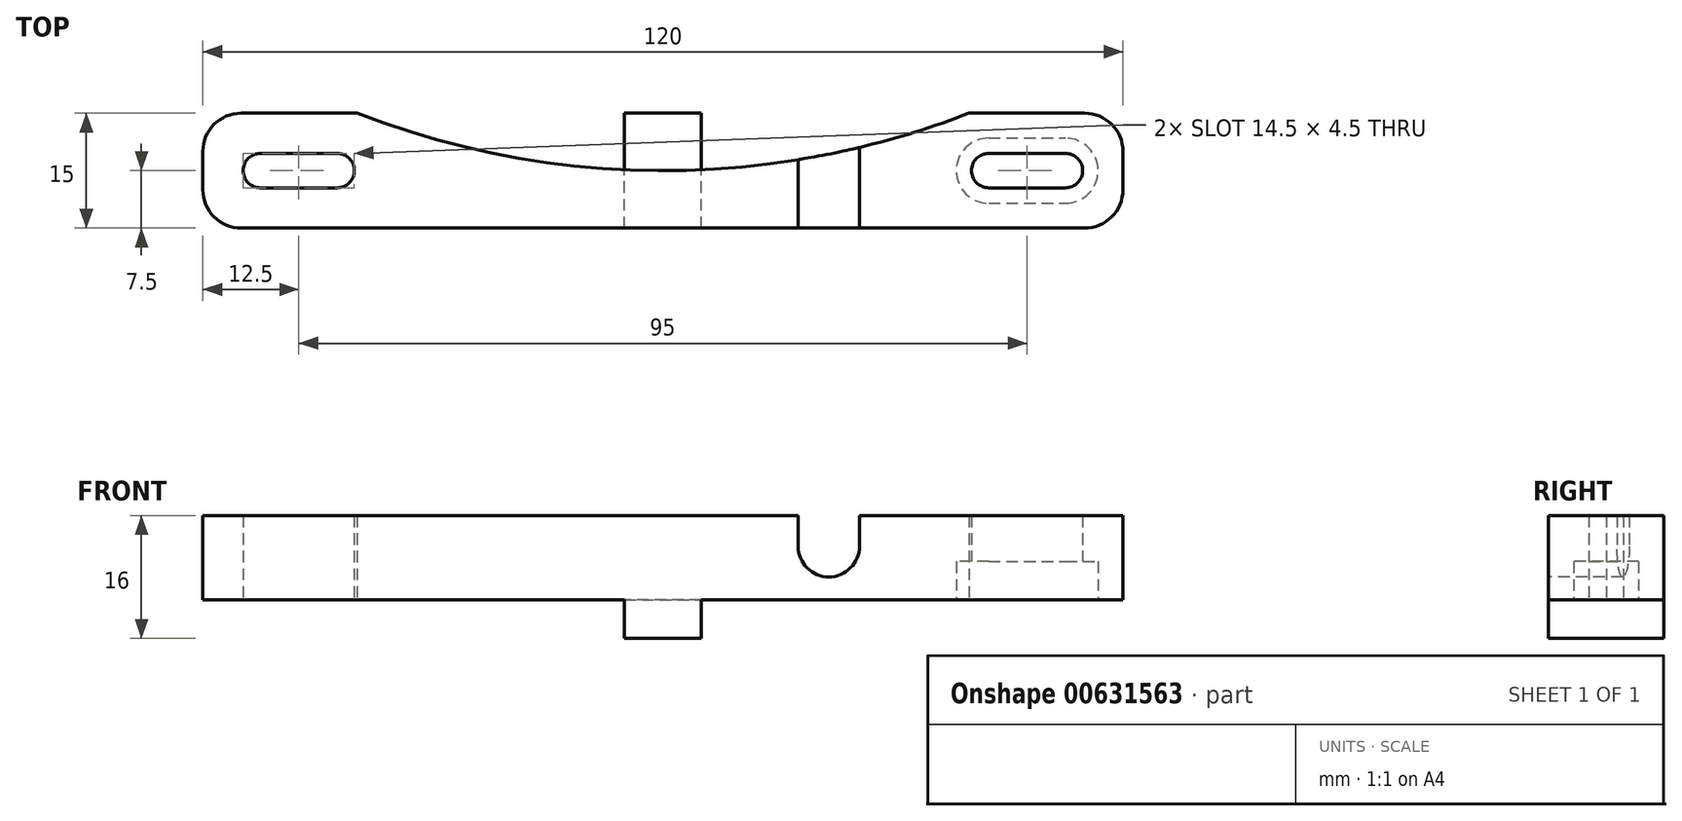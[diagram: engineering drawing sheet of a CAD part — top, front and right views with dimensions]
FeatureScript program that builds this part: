
annotation { "Feature Type Name" : "Feature", "Feature Type Description" : "" }
export const myFeature = defineFeature(function(context is Context, id is Id, definition is map)
    precondition{}
    {
        {
            var Q0;
            Q0=qCreatedBy(makeId("Top.planeOp"),FACE);
            var sketch = newSketch(context, id + "F0", { "sketchPlane" : qUnion([Q0])});
            skLineSegment(sketch, "E0.bottom", {"start": v(55, -7.5) * mm, "end": v(-55, -7.5) * mm});
            skLineSegment(sketch, "E0.top", {"start": v(55, 7.5) * mm, "end": v(-55, 7.5) * mm});
            skLineSegment(sketch, "E0.left", {"start": v(60, -2.5) * mm, "end": v(60, 2.5) * mm});
            skLineSegment(sketch, "E0.right", {"start": v(-60, -2.5) * mm, "end": v(-60, 2.5) * mm});
            skPoint(sketch, "E0.middle", {"position": v(0, 0) * mm});
            skLineSegment(sketch, "E1.left", {"start": v(5, -7.5) * mm, "end": v(5, 7.5) * mm});
            skLineSegment(sketch, "E1.right", {"start": v(-5, -7.5) * mm, "end": v(-5, 7.5) * mm});
            skPoint(sketch, "E2.orphan", {"position": v(-5, -15) * mm});
            skPoint(sketch, "E3.orphan", {"position": v(5, -15) * mm});
            skArc(sketch, "E4", {"start": v(-52.5, 2.25) * mm, "mid": v(-54.75, 0) * mm, "end": v(-52.5, -2.25) * mm});
            skArc(sketch, "E5", {"start": v(52.5, -2.25) * mm, "mid": v(54.75, 0) * mm, "end": v(52.5, 2.25) * mm});
            skArc(sketch, "E6", {"start": v(42.5, 2.25) * mm, "mid": v(40.25, 0) * mm, "end": v(42.5, -2.25) * mm});
            skArc(sketch, "E7", {"start": v(-42.5, -2.25) * mm, "mid": v(-40.25, 0) * mm, "end": v(-42.5, 2.25) * mm});
            skLineSegment(sketch, "E8", {"start": v(42.5, 2.25) * mm, "end": v(52.5, 2.25) * mm});
            skLineSegment(sketch, "E9", {"start": v(42.5, -2.25) * mm, "end": v(52.5, -2.25) * mm});
            skLineSegment(sketch, "E10", {"start": v(-52.5, -2.25) * mm, "end": v(-42.5, -2.25) * mm});
            skLineSegment(sketch, "E11", {"start": v(-42.5, 2.25) * mm, "end": v(-52.5, 2.25) * mm});
            skPoint(sketch, "E12.visualSharp", {"position": v(60, 7.5) * mm});
            skArc(sketch, "E12.filletArc", {"start": v(60, 2.5) * mm, "mid": v(58.54, 6.04) * mm, "end": v(55, 7.5) * mm});
            skPoint(sketch, "E13.visualSharp", {"position": v(60, -7.5) * mm});
            skArc(sketch, "E13.filletArc", {"start": v(55, -7.5) * mm, "mid": v(58.54, -6.04) * mm, "end": v(60, -2.5) * mm});
            skPoint(sketch, "E14.visualSharp", {"position": v(-60, -7.5) * mm});
            skArc(sketch, "E14.filletArc", {"start": v(-60, -2.5) * mm, "mid": v(-58.54, -6.04) * mm, "end": v(-55, -7.5) * mm});
            skPoint(sketch, "E15.visualSharp", {"position": v(-60, 7.5) * mm});
            skArc(sketch, "E15.filletArc", {"start": v(-55, 7.5) * mm, "mid": v(-58.54, 6.04) * mm, "end": v(-60, 2.5) * mm});
            skArc(sketch, "E16", {"start": v(-39.92, 7.5) * mm, "mid": v(0, 0) * mm, "end": v(39.92, 7.5) * mm});
            skPoint(sketch, "E17.orphan", {"position": v(-5, 15) * mm});
            skPoint(sketch, "E18.orphan", {"position": v(5, 15) * mm});
            skSolve(sketch);
        }
        {
            var Q0;
            {var subQ0=sQuery(id+"F0.wireOp",EDGE,"E1.left");var subQ1=sQuery(id+"F0.wireOp",EDGE,"E0.top");var subQ2=makeQuery(id+"F0.imprint","INTERSECT",VERTEX,{"derivedFrom":[subQ1,subQ0]});Q0=makeQuery(id+"F0.imprint","IMPRINT",FACE,{"disambiguationData":[TD([[makeQuery(id+"F0.imprint","IMPRINT",EDGE,{"disambiguationData":[TD([[subQ2,-1.0]])],"derivedFrom":subQ1}),1.0]])]});}
            var Q1;
            {var subQ0=sQuery(id+"F0.wireOp",EDGE,"E1.left");var subQ1=sQuery(id+"F0.wireOp",EDGE,"E0.bottom");var subQ2=makeQuery(id+"F0.imprint","INTERSECT",VERTEX,{"derivedFrom":[subQ1,subQ0]});Q1=makeQuery(id+"F0.imprint","IMPRINT",FACE,{"disambiguationData":[TD([[makeQuery(id+"F0.imprint","IMPRINT",EDGE,{"disambiguationData":[TD([[subQ2,-1.0]])],"derivedFrom":subQ1}),-1.0]])]});}
            extrude(context, id + "F1", {"entities" : qUnion([Q0, Q1]), "depth" : 5 * mm, "offsetDistance" : 25 * mm});
        }
        {
            var Q0;
            Q0=makeQuery(id+"F1.opExtrude","CAP_FACE",FACE,{"disambiguationData":[OSD([sQuery(id+"F0.wireOp",EDGE,"E0.bottom"),sQuery(id+"F0.wireOp",EDGE,"E0.top"),sQuery(id+"F0.wireOp",EDGE,"E1.left"),sQuery(id+"F0.wireOp",EDGE,"E1.right")])],"isStart":false});
            var sketch = newSketch(context, id + "F2", { "sketchPlane" : qUnion([Q0])});
            skArc(sketch, "E19.0", {"start": v(-39.92, 7.5) * mm, "mid": v(0, 0) * mm, "end": v(39.92, 7.5) * mm});
            skLineSegment(sketch, "E20.0", {"start": v(55, 7.5) * mm, "end": v(-55, 7.5) * mm});
            skLineSegment(sketch, "E21.0", {"start": v(55, -7.5) * mm, "end": v(-55, -7.5) * mm});
            skArc(sketch, "E22.0", {"start": v(-55, 7.5) * mm, "mid": v(-58.54, 6.04) * mm, "end": v(-60, 2.5) * mm});
            skLineSegment(sketch, "E22.1", {"start": v(-60, -2.5) * mm, "end": v(-60, 2.5) * mm});
            skArc(sketch, "E22.2", {"start": v(-60, -2.5) * mm, "mid": v(-58.54, -6.04) * mm, "end": v(-55, -7.5) * mm});
            skLineSegment(sketch, "E23.0", {"start": v(-52.5, -2.25) * mm, "end": v(-42.5, -2.25) * mm});
            skArc(sketch, "E23.1", {"start": v(-52.5, 2.25) * mm, "mid": v(-54.75, 0) * mm, "end": v(-52.5, -2.25) * mm});
            skLineSegment(sketch, "E23.2", {"start": v(-42.5, 2.25) * mm, "end": v(-52.5, 2.25) * mm});
            skArc(sketch, "E23.3", {"start": v(-42.5, -2.25) * mm, "mid": v(-40.25, 0) * mm, "end": v(-42.5, 2.25) * mm});
            skArc(sketch, "E24.0", {"start": v(52.5, -2.25) * mm, "mid": v(54.75, 0) * mm, "end": v(52.5, 2.25) * mm});
            skLineSegment(sketch, "E24.1", {"start": v(42.5, 2.25) * mm, "end": v(52.5, 2.25) * mm});
            skLineSegment(sketch, "E24.2", {"start": v(42.5, -2.25) * mm, "end": v(52.5, -2.25) * mm});
            skArc(sketch, "E24.3", {"start": v(42.5, 2.25) * mm, "mid": v(40.25, 0) * mm, "end": v(42.5, -2.25) * mm});
            skArc(sketch, "E24.4", {"start": v(55, -7.5) * mm, "mid": v(58.54, -6.04) * mm, "end": v(60, -2.5) * mm});
            skLineSegment(sketch, "E24.5", {"start": v(60, -2.5) * mm, "end": v(60, 2.5) * mm});
            skArc(sketch, "E24.6", {"start": v(60, 2.5) * mm, "mid": v(58.54, 6.04) * mm, "end": v(55, 7.5) * mm});
            skSolve(sketch);
        }
        {
            var Q0;
            {var subQ7=sQuery(id+"F2.wireOp",EDGE,"E22.0");Q0=makeQuery(id+"F2.imprint","IMPRINT",FACE,{"disambiguationData":[TD([[makeQuery(id+"F2.imprint","IMPRINT",EDGE,{"derivedFrom":subQ7}),1.0]])]});}
            var Q1;
            Q1=makeQuery(id+"F2.imprint","IMPRINT",FACE,{"disambiguationData":[TD([[makeQuery(id+"F2.imprint","IMPRINT",EDGE,{"derivedFrom":sQuery(id+"F2.wireOp",EDGE,"E24.0")}),-1.0]])]});
            var Q2;
            {var subQ0=sQuery(id+"F2.wireOp",EDGE,"E19.0");var subQ1=makeQuery(id+"F1.opExtrude","CAP_EDGE",EDGE,{"disambiguationData":[OSD([sQuery(id+"F0.wireOp",EDGE,"E1.right")])],"isStart":false});var subQ2=makeQuery(id+"F2.imprint","INTERSECT",VERTEX,{"derivedFrom":[subQ1,subQ0]});Q2=makeQuery(id+"F2.imprint","IMPRINT",FACE,{"disambiguationData":[TD([[makeQuery(id+"F2.imprint","IMPRINT",EDGE,{"disambiguationData":[TD([[subQ2,-1.0]])],"derivedFrom":subQ0}),-1.0]])]});}
            extrude(context, id + "F3", {"entities" : qUnion([Q0, Q1, Q2]), "operationType" : NewBodyOperationType.ADD, "oppositeDirection" : true, "depth" : 0 * mm, "offsetDistance" : 25 * mm, "hasSecondDirection" : true, "secondDirectionOppositeDirection" : false, "secondDirectionDepth" : 11 * mm});
        }
        {
            var Q0;
            {var subQ0=sQuery(id+"F2.wireOp",EDGE,"E24.2");var subQ1=sQuery(id+"F2.wireOp",EDGE,"E24.0");var subQ2=sQuery(id+"F2.wireOp",EDGE,"E24.3");var subQ3=sQuery(id+"F2.wireOp",EDGE,"E21.0");var subQ5=sQuery(id+"F2.wireOp",EDGE,"E24.6");var subQ6=sQuery(id+"F0.wireOp",EDGE,"E1.left");var subQ7=sQuery(id+"F2.wireOp",EDGE,"E24.1");var subQ8=sQuery(id+"F2.wireOp",EDGE,"E20.0");var subQ9=sQuery(id+"F2.wireOp",EDGE,"E19.0");var subQ10=sQuery(id+"F2.wireOp",EDGE,"E24.4");var subQ11=sQuery(id+"F2.wireOp",EDGE,"E24.5");Q0=makeQuery(id+"F3.boolean.opBoolean","SPLIT",FACE,{"disambiguationData":[TD([makeQuery(id+"F1.opExtrude","SWEPT_FACE",FACE,{"disambiguationData":[OSD([subQ6])]})])],"derivedFrom":makeQuery(id+"F3.opExtrude","CAP_FACE",FACE,{"disambiguationData":[OSD([subQ9,subQ8,subQ3,sQuery(id+"F2.wireOp",EDGE,"E22.0"),sQuery(id+"F2.wireOp",EDGE,"E22.1"),sQuery(id+"F2.wireOp",EDGE,"E22.2"),sQuery(id+"F2.wireOp",EDGE,"E23.0"),sQuery(id+"F2.wireOp",EDGE,"E23.1"),sQuery(id+"F2.wireOp",EDGE,"E23.2"),sQuery(id+"F2.wireOp",EDGE,"E23.3"),subQ1,subQ7,subQ0,subQ2,subQ10,subQ11,subQ5])],"isStart":false})});}
            var sketch = newSketch(context, id + "F4", { "sketchPlane" : qUnion([Q0])});
            skLineSegment(sketch, "E25.0", {"start": v(42.5, -2.25) * mm, "end": v(52.5, -2.25) * mm});
            skArc(sketch, "E25.1", {"start": v(42.5, -2.25) * mm, "mid": v(40.25, 0) * mm, "end": v(42.5, 2.25) * mm});
            skLineSegment(sketch, "E25.2", {"start": v(42.5, 2.25) * mm, "end": v(52.5, 2.25) * mm});
            skArc(sketch, "E25.3", {"start": v(52.5, 2.25) * mm, "mid": v(54.75, 0) * mm, "end": v(52.5, -2.25) * mm});
            skArc(sketch, "E26.0", {"start": v(52.5, 4.25) * mm, "mid": v(56.75, 0) * mm, "end": v(52.5, -4.25) * mm});
            skLineSegment(sketch, "E26.1", {"start": v(42.5, 4.25) * mm, "end": v(52.5, 4.25) * mm});
            skArc(sketch, "E26.2", {"start": v(42.5, -4.25) * mm, "mid": v(38.25, 0) * mm, "end": v(42.5, 4.25) * mm});
            skLineSegment(sketch, "E26.3", {"start": v(42.5, -4.25) * mm, "end": v(52.5, -4.25) * mm});
            skArc(sketch, "E27.0", {"start": v(-42.5, 2.25) * mm, "mid": v(-40.25, 0) * mm, "end": v(-42.5, -2.25) * mm});
            skLineSegment(sketch, "E27.1", {"start": v(-52.5, 2.25) * mm, "end": v(-42.5, 2.25) * mm});
            skArc(sketch, "E27.2", {"start": v(-52.5, -2.25) * mm, "mid": v(-54.75, 0) * mm, "end": v(-52.5, 2.25) * mm});
            skLineSegment(sketch, "E27.3", {"start": v(-42.5, -2.25) * mm, "end": v(-52.5, -2.25) * mm});
            skArc(sketch, "E28.0", {"start": v(-42.5, 4.25) * mm, "mid": v(-38.25, 0) * mm, "end": v(-42.5, -4.25) * mm});
            skLineSegment(sketch, "E28.1", {"start": v(-52.5, 4.25) * mm, "end": v(-42.5, 4.25) * mm});
            skArc(sketch, "E28.2", {"start": v(-52.5, -4.25) * mm, "mid": v(-56.75, 0) * mm, "end": v(-52.5, 4.25) * mm});
            skLineSegment(sketch, "E28.3", {"start": v(-42.5, -4.25) * mm, "end": v(-52.5, -4.25) * mm});
            skSolve(sketch);
        }
        {
            var Q0;
            Q0=makeQuery(id+"F4.imprint","IMPRINT",FACE,{"disambiguationData":[TD([[makeQuery(id+"F4.imprint","IMPRINT",EDGE,{"derivedFrom":sQuery(id+"F4.wireOp",EDGE,"E27.0")}),1.0]])]});
            var Q1;
            Q1=makeQuery(id+"F4.imprint","IMPRINT",FACE,{"disambiguationData":[TD([[makeQuery(id+"F4.imprint","IMPRINT",EDGE,{"derivedFrom":sQuery(id+"F4.wireOp",EDGE,"E25.0")}),-1.0]])]});
            extrude(context, id + "F5", {"entities" : qUnion([Q0, Q1]), "operationType" : NewBodyOperationType.REMOVE, "oppositeDirection" : true, "depth" : 5 * mm, "offsetDistance" : 25 * mm});
        }
        {
            var Q0;
            Q0=makeQuery(id+"F3.boolean.opBoolean","MERGE",FACE,{"derivedFrom":[makeQuery(id+"F1.opExtrude","SWEPT_FACE",FACE,{"disambiguationData":[OSD([sQuery(id+"F0.wireOp",EDGE,"E0.bottom")])]}),makeQuery(id+"F3.opExtrude","SWEPT_FACE",FACE,{"disambiguationData":[OSD([sQuery(id+"F2.wireOp",EDGE,"E21.0")])]})]});
            var sketch = newSketch(context, id + "F6", { "sketchPlane" : qUnion([Q0])});
            skLineSegment(sketch, "E29.0", {"start": v(-5, 5) * mm, "end": v(-55, 5) * mm});
            skLineSegment(sketch, "E29.1", {"start": v(55, 16) * mm, "end": v(-55, 16) * mm});
            skLineSegment(sketch, "E29.2", {"start": v(-5, 5) * mm, "end": v(-5, 0) * mm});
            skLineSegment(sketch, "E30.0", {"start": v(5, 5) * mm, "end": v(5, 0) * mm});
            skArc(sketch, "E31", {"start": v(17.64, 12) * mm, "mid": v(21.64, 8) * mm, "end": v(25.64, 12) * mm});
            skLineSegment(sketch, "E32", {"start": v(17.64, 12) * mm, "end": v(17.64, 16) * mm});
            skLineSegment(sketch, "E33", {"start": v(25.64, 12) * mm, "end": v(25.64, 16) * mm});
            skLineSegment(sketch, "E34", {"start": v(25.64, 16) * mm, "end": v(17.64, 16) * mm});
            skSolve(sketch);
        }
        {
            var Q0;
            Q0=makeQuery(id+"F6.imprint","IMPRINT",FACE,{"disambiguationData":[TD([[makeQuery(id+"F6.imprint","IMPRINT",EDGE,{"derivedFrom":sQuery(id+"F6.wireOp",EDGE,"E31")}),1.0]])]});
            extrude(context, id + "F7", {"entities" : qUnion([Q0]), "operationType" : NewBodyOperationType.REMOVE, "endBound" : BoundingType.THROUGH_ALL, "oppositeDirection" : true, "depth" : 25 * mm, "offsetDistance" : 25 * mm});
        }
    });
